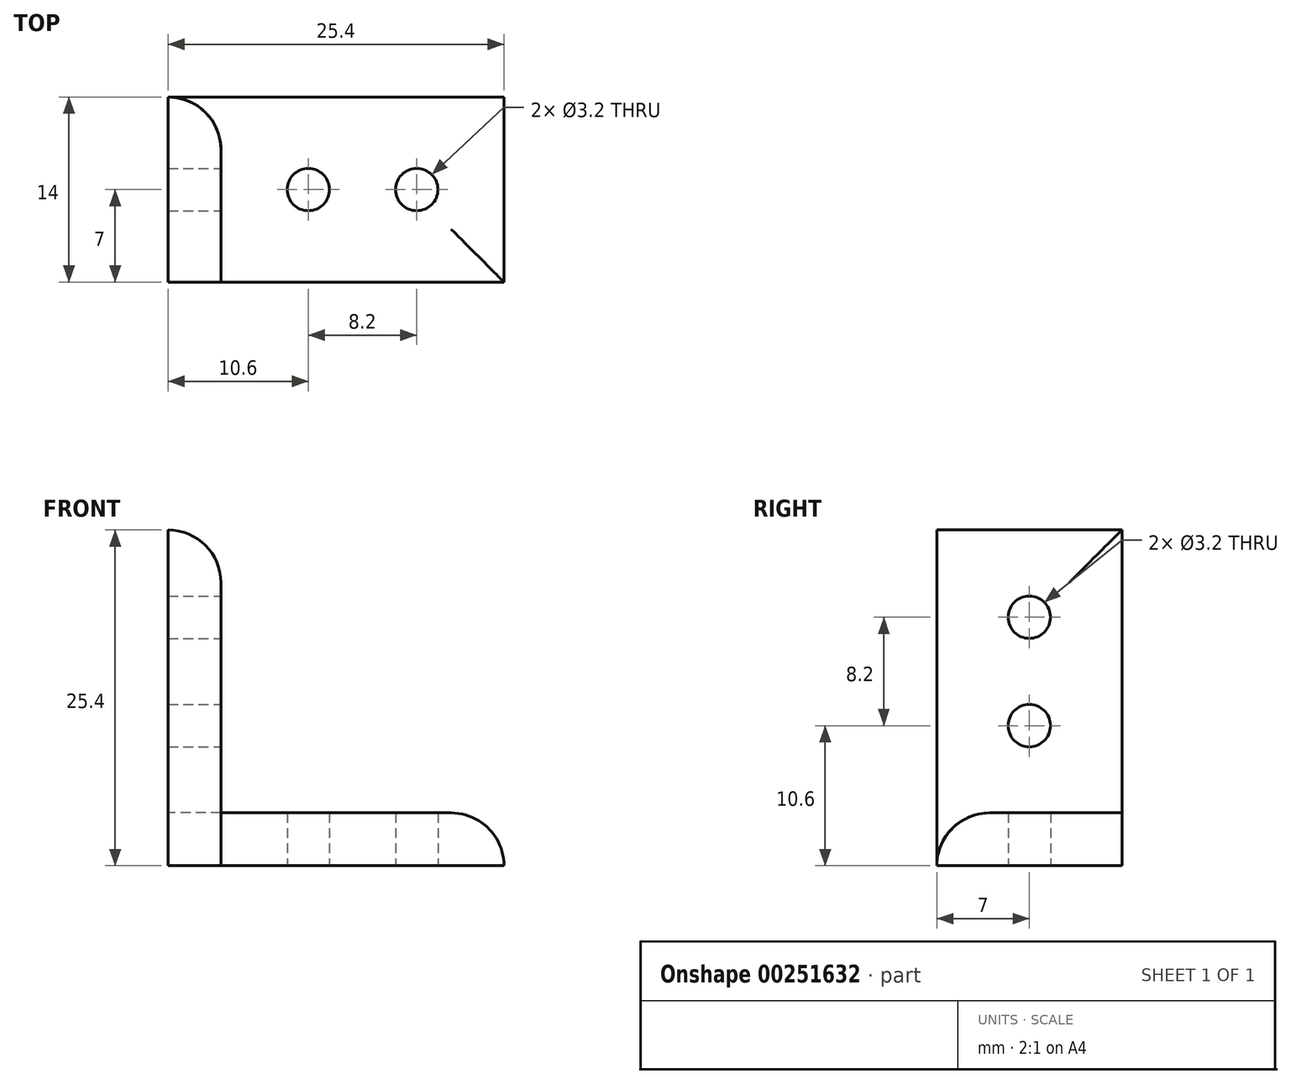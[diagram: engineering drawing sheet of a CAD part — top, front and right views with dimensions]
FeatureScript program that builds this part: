
annotation { "Feature Type Name" : "Feature", "Feature Type Description" : "" }
export const myFeature = defineFeature(function(context is Context, id is Id, definition is map)
    precondition{}
    {
        {
            var Q0;
            Q0=qCreatedBy(makeId("Top.planeOp"),FACE);
            var sketch = newSketch(context, id + "F0", { "sketchPlane" : qUnion([Q0])});
            skCircle(sketch, "E0", {"center": v(0, 0) * mm, "radius": 1.6 * mm});
            skCircle(sketch, "E1", {"center": v(8.2, 0) * mm, "radius": 1.6 * mm});
            skLineSegment(sketch, "E2.bottom", {"start": v(-6.6, 7) * mm, "end": v(14.8, 7) * mm});
            skLineSegment(sketch, "E2.top", {"start": v(-6.6, -7) * mm, "end": v(14.8, -7) * mm});
            skLineSegment(sketch, "E2.left", {"start": v(-6.6, 7) * mm, "end": v(-6.6, -7) * mm});
            skLineSegment(sketch, "E2.right", {"start": v(14.8, 7) * mm, "end": v(14.8, -7) * mm});
            skLineSegment(sketch, "E3", {"start": v(-6.6, 0) * mm, "end": v(14.8, 0) * mm, "construction": true});
            skLineSegment(sketch, "E4", {"start": v(-6.6, 7) * mm, "end": v(-10.6, 7) * mm});
            skLineSegment(sketch, "E5", {"start": v(-10.6, 7) * mm, "end": v(-10.6, -7) * mm});
            skLineSegment(sketch, "E6", {"start": v(-10.6, -7) * mm, "end": v(-6.6, -7) * mm});
            skSolve(sketch);
        }
        {
            var Q0;
            Q0=makeQuery(id+"F0.imprint","IMPRINT",FACE,{"disambiguationData":[TD([[makeQuery(id+"F0.imprint","IMPRINT",EDGE,{"derivedFrom":sQuery(id+"F0.wireOp",EDGE,"E2.left")}),-1.0]])]});
            extrude(context, id + "F1", {"entities" : qUnion([Q0]), "depth" : 25.4 * mm, "offsetDistance" : 25 * mm});
        }
        {
            var Q0;
            Q0=makeQuery(id+"F0.imprint","IMPRINT",FACE,{"disambiguationData":[TD([[makeQuery(id+"F0.imprint","IMPRINT",EDGE,{"derivedFrom":sQuery(id+"F0.wireOp",EDGE,"E0")}),-1.0]])]});
            extrude(context, id + "F2", {"entities" : qUnion([Q0]), "operationType" : NewBodyOperationType.ADD, "depth" : 4 * mm, "offsetDistance" : 25 * mm});
        }
        {
            var Q0;
            Q0=makeQuery(id+"F1.opExtrude","SWEPT_FACE",FACE,{"disambiguationData":[OSD([sQuery(id+"F0.wireOp",EDGE,"E2.left")])]});
            var sketch = newSketch(context, id + "F3", { "sketchPlane" : qUnion([Q0])});
            skLineSegment(sketch, "E7", {"start": v(0, 25.4) * mm, "end": v(0, 4) * mm, "construction": true});
            skCircle(sketch, "E8", {"center": v(0, 18.8) * mm, "radius": 1.6 * mm});
            skCircle(sketch, "E9", {"center": v(0, 10.6) * mm, "radius": 1.6 * mm});
            skSolve(sketch);
        }
        {
            var Q0;
            Q0=makeQuery(id+"F3.imprint","IMPRINT",FACE,{"disambiguationData":[TD([[makeQuery(id+"F3.imprint","IMPRINT",EDGE,{"derivedFrom":sQuery(id+"F3.wireOp",EDGE,"E8")}),1.0]])]});
            var Q1;
            Q1=makeQuery(id+"F3.imprint","IMPRINT",FACE,{"disambiguationData":[TD([[makeQuery(id+"F3.imprint","IMPRINT",EDGE,{"derivedFrom":sQuery(id+"F3.wireOp",EDGE,"E9")}),1.0]])]});
            var Q2;
            Q2=makeQuery(id+"F1.opExtrude","SWEPT_FACE",FACE,{"disambiguationData":[OSD([sQuery(id+"F0.wireOp",EDGE,"E5")])]});
            extrude(context, id + "F4", {"entities" : qUnion([Q0, Q1]), "operationType" : NewBodyOperationType.REMOVE, "endBound" : BoundingType.UP_TO_SURFACE, "oppositeDirection" : true, "depth" : 25 * mm, "endBoundEntityFace" : qUnion([Q2]), "offsetDistance" : 25 * mm});
        }
        {
            var Q0;
            Q0=makeQuery(id+"F2.opExtrude","CAP_EDGE",EDGE,{"disambiguationData":[OSD([sQuery(id+"F0.wireOp",EDGE,"E2.left")])],"isStart":false});
            var Q1;
            Q1=makeQuery(id+"F1.opExtrude","CAP_EDGE",EDGE,{"disambiguationData":[OSD([sQuery(id+"F0.wireOp",EDGE,"E2.left")])],"isStart":false});
            var Q2;
            Q2=makeQuery(id+"F2.opExtrude","CAP_EDGE",EDGE,{"disambiguationData":[OSD([sQuery(id+"F0.wireOp",EDGE,"E2.right")])],"isStart":false});
            var Q3;
            Q3=makeQuery(id+"F1.opExtrude","SWEPT_EDGE",EDGE,{"disambiguationData":[OSD([sQuery(id+"F0.wireOp",EDGE,"E2.bottom"),sQuery(id+"F0.wireOp",EDGE,"E2.left"),sQuery(id+"F0.wireOp",EDGE,"E4")])]});
            var Q4;
            Q4=makeQuery(id+"F2.opExtrude","CAP_EDGE",EDGE,{"disambiguationData":[OSD([sQuery(id+"F0.wireOp",EDGE,"E2.top")])],"isStart":false});
            fillet(context, id + "F5", {"entities" : qUnion([Q0, Q1, Q2, Q3, Q4]), "radius" : 4 * mm, "tangentPropagation" : true, "allowEdgeOverflow" : false});
        }
    });
